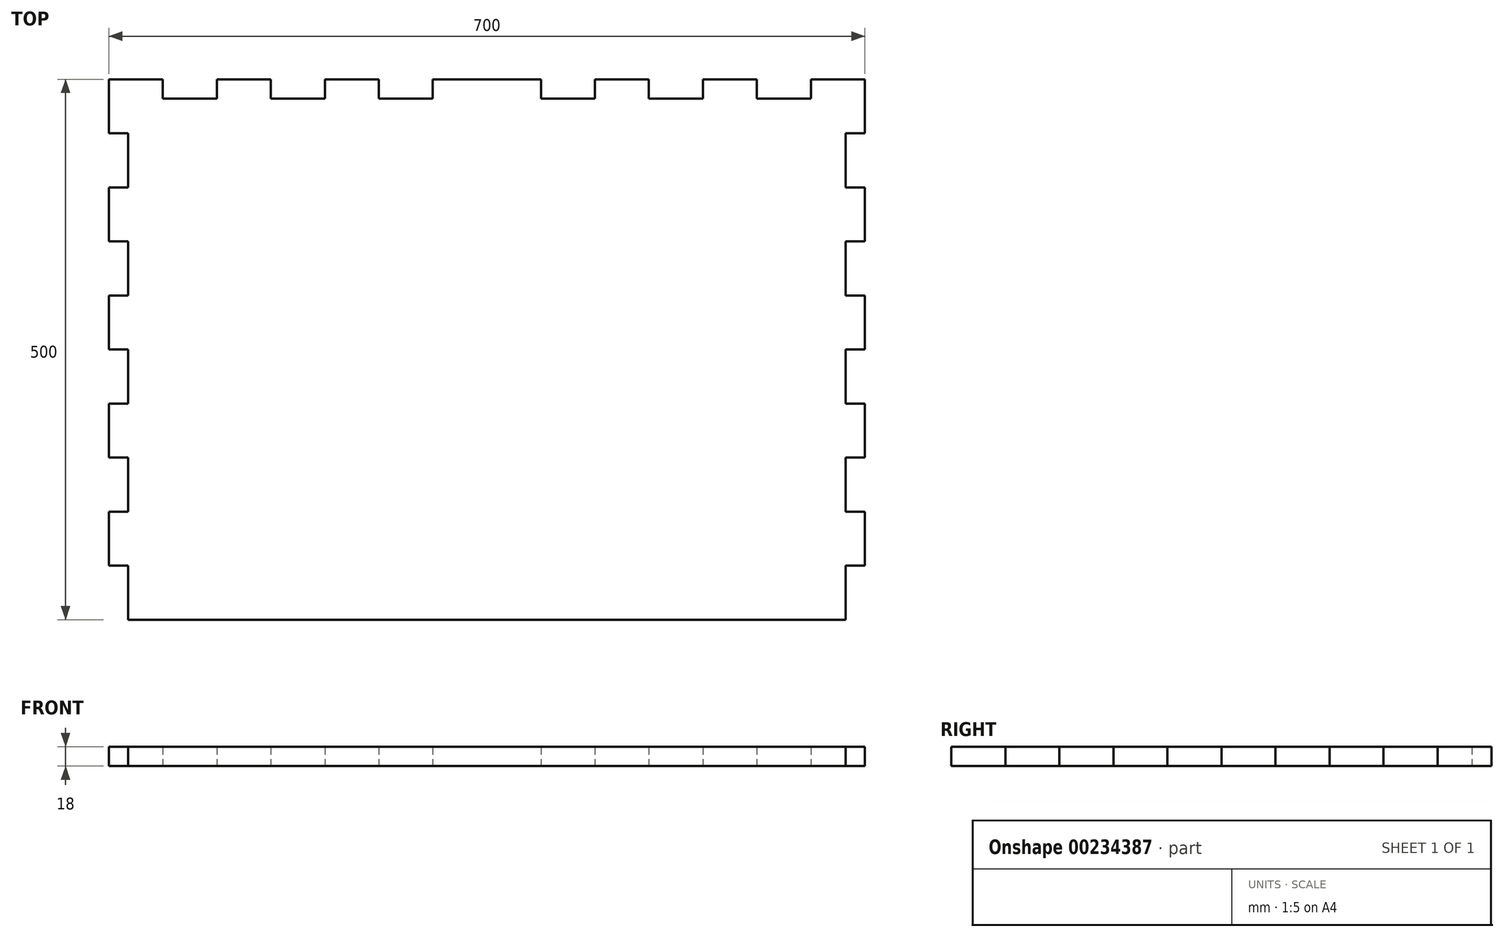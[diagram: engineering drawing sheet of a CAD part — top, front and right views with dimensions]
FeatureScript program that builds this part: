
annotation { "Feature Type Name" : "Feature", "Feature Type Description" : "" }
export const myFeature = defineFeature(function(context is Context, id is Id, definition is map)
    precondition{}
    {
        {
            var Q0;
            Q0=qCreatedBy(makeId("Top.planeOp"),FACE);
            var sketch = newSketch(context, id + "F0", { "sketchPlane" : qUnion([Q0])});
            skLineSegment(sketch, "E0.left", {"start": v(-350, -175) * mm, "end": v(-350, -125) * mm});
            skPoint(sketch, "E0.middle", {"position": v(0, 0) * mm});
            skLineSegment(sketch, "E1.right", {"start": v(-250, 157) * mm, "end": v(-250, 175) * mm});
            skLineSegment(sketch, "E2.right", {"start": v(-200, 157) * mm, "end": v(-200, 175) * mm});
            skLineSegment(sketch, "E3.right", {"start": v(-150, 157) * mm, "end": v(-150, 175) * mm});
            skLineSegment(sketch, "E4.right", {"start": v(-100, 157) * mm, "end": v(-100, 175) * mm});
            skLineSegment(sketch, "E5.right", {"start": v(-50, 157) * mm, "end": v(-50, 175) * mm});
            skLineSegment(sketch, "E6.top", {"start": v(0, 175) * mm, "end": v(50, 175) * mm});
            skLineSegment(sketch, "E6.right", {"start": v(50, 157) * mm, "end": v(50, 175) * mm});
            skLineSegment(sketch, "E7.bottom", {"start": v(50, 157) * mm, "end": v(100, 157) * mm});
            skLineSegment(sketch, "E7.right", {"start": v(100, 157) * mm, "end": v(100, 175) * mm});
            skLineSegment(sketch, "E8.top", {"start": v(100, 175) * mm, "end": v(150, 175) * mm});
            skLineSegment(sketch, "E8.right", {"start": v(150, 157) * mm, "end": v(150, 175) * mm});
            skLineSegment(sketch, "E9.bottom", {"start": v(150, 157) * mm, "end": v(200, 157) * mm});
            skLineSegment(sketch, "E9.right", {"start": v(200, 157) * mm, "end": v(200, 175) * mm});
            skLineSegment(sketch, "E10.top", {"start": v(200, 175) * mm, "end": v(250, 175) * mm});
            skLineSegment(sketch, "E10.right", {"start": v(250, 157) * mm, "end": v(250, 175) * mm});
            skLineSegment(sketch, "E11.bottom", {"start": v(250, 157) * mm, "end": v(300, 157) * mm});
            skLineSegment(sketch, "E11.right", {"start": v(300, 157) * mm, "end": v(300, 175) * mm});
            skLineSegment(sketch, "E12.top", {"start": v(300, 175) * mm, "end": v(350, 175) * mm});
            skLineSegment(sketch, "E12.right", {"start": v(350, 157) * mm, "end": v(350, 175) * mm});
            skPoint(sketch, "E13.orphan", {"position": v(-350, 175) * mm});
            skLineSegment(sketch, "E14.top", {"start": v(-332, -325) * mm, "end": v(332, -325) * mm});
            skLineSegment(sketch, "E14.right", {"start": v(350, -225) * mm, "end": v(350, -275) * mm});
            skLineSegment(sketch, "E15.top", {"start": v(-332, -275) * mm, "end": v(-350, -275) * mm});
            skLineSegment(sketch, "E15.left", {"start": v(-332, -325) * mm, "end": v(-332, -275) * mm});
            skLineSegment(sketch, "E16.top", {"start": v(-332, -225) * mm, "end": v(-350, -225) * mm});
            skLineSegment(sketch, "E16.right", {"start": v(-350, -275) * mm, "end": v(-350, -225) * mm});
            skLineSegment(sketch, "E17.top", {"start": v(-332, -175) * mm, "end": v(-350, -175) * mm});
            skLineSegment(sketch, "E17.left", {"start": v(-332, -225) * mm, "end": v(-332, -175) * mm});
            skLineSegment(sketch, "E18.top", {"start": v(-332, -125) * mm, "end": v(-350, -125) * mm});
            skLineSegment(sketch, "E19.top", {"start": v(-332, -75) * mm, "end": v(-350, -75) * mm});
            skLineSegment(sketch, "E19.left", {"start": v(-332, -125) * mm, "end": v(-332, -75) * mm});
            skLineSegment(sketch, "E20.top", {"start": v(-332, -25) * mm, "end": v(-350, -25) * mm});
            skLineSegment(sketch, "E20.right", {"start": v(-350, -75) * mm, "end": v(-350, -25) * mm});
            skLineSegment(sketch, "E21.top", {"start": v(-332, 25) * mm, "end": v(-350, 25) * mm});
            skLineSegment(sketch, "E21.left", {"start": v(-332, -25) * mm, "end": v(-332, 25) * mm});
            skLineSegment(sketch, "E22.top", {"start": v(-332, 75) * mm, "end": v(-350, 75) * mm});
            skLineSegment(sketch, "E22.right", {"start": v(-350, 25) * mm, "end": v(-350, 75) * mm});
            skLineSegment(sketch, "E23.top", {"start": v(-332, 125) * mm, "end": v(-350, 125) * mm});
            skLineSegment(sketch, "E23.left", {"start": v(-332, 75) * mm, "end": v(-332, 125) * mm});
            skLineSegment(sketch, "E24.trimOffspring", {"start": v(-350, 125) * mm, "end": v(-350, 157) * mm});
            skLineSegment(sketch, "E25.top", {"start": v(332, -275) * mm, "end": v(350, -275) * mm});
            skLineSegment(sketch, "E25.left", {"start": v(332, -325) * mm, "end": v(332, -275) * mm});
            skLineSegment(sketch, "E26.top", {"start": v(332, -225) * mm, "end": v(350, -225) * mm});
            skLineSegment(sketch, "E26.right", {"start": v(350, -275) * mm, "end": v(350, -225) * mm});
            skLineSegment(sketch, "E27.top", {"start": v(332, -175) * mm, "end": v(350, -175) * mm});
            skLineSegment(sketch, "E27.left", {"start": v(332, -225) * mm, "end": v(332, -175) * mm});
            skLineSegment(sketch, "E28.top", {"start": v(332, -125) * mm, "end": v(350, -125) * mm});
            skLineSegment(sketch, "E28.right", {"start": v(350, -175) * mm, "end": v(350, -125) * mm});
            skLineSegment(sketch, "E29.top", {"start": v(332, -75) * mm, "end": v(350, -75) * mm});
            skLineSegment(sketch, "E29.left", {"start": v(332, -125) * mm, "end": v(332, -75) * mm});
            skLineSegment(sketch, "E30.top", {"start": v(332, -25) * mm, "end": v(350, -25) * mm});
            skLineSegment(sketch, "E30.right", {"start": v(350, -75) * mm, "end": v(350, -25) * mm});
            skLineSegment(sketch, "E31.top", {"start": v(332, 25) * mm, "end": v(350, 25) * mm});
            skLineSegment(sketch, "E31.left", {"start": v(332, -25) * mm, "end": v(332, 25) * mm});
            skLineSegment(sketch, "E32.top", {"start": v(332, 75) * mm, "end": v(350, 75) * mm});
            skLineSegment(sketch, "E32.right", {"start": v(350, 25) * mm, "end": v(350, 75) * mm});
            skLineSegment(sketch, "E33.top", {"start": v(332, 125) * mm, "end": v(350, 125) * mm});
            skLineSegment(sketch, "E33.left", {"start": v(332, 75) * mm, "end": v(332, 125) * mm});
            skLineSegment(sketch, "E34.trimOffspring", {"start": v(350, 125) * mm, "end": v(350, 175) * mm});
            skPoint(sketch, "E0.right.start.orphan", {"position": v(350, -175) * mm});
            skPoint(sketch, "E35.orphan", {"position": v(350, -325) * mm});
            skLineSegment(sketch, "E36", {"start": v(-350, 157) * mm, "end": v(-350, 175) * mm});
            skLineSegment(sketch, "E37", {"start": v(-300, 175) * mm, "end": v(-350, 175) * mm});
            skLineSegment(sketch, "E38", {"start": v(-300, 175) * mm, "end": v(-300, 157) * mm});
            skLineSegment(sketch, "E39", {"start": v(-300, 157) * mm, "end": v(-250, 157) * mm});
            skLineSegment(sketch, "E40", {"start": v(-200, 157) * mm, "end": v(-150, 157) * mm});
            skLineSegment(sketch, "E41", {"start": v(-250, 175) * mm, "end": v(-200, 175) * mm});
            skLineSegment(sketch, "E42", {"start": v(-150, 175) * mm, "end": v(-100, 175) * mm});
            skLineSegment(sketch, "E43", {"start": v(-100, 157) * mm, "end": v(-50, 157) * mm});
            skLineSegment(sketch, "E44", {"start": v(-50, 175) * mm, "end": v(0, 175) * mm});
            skSolve(sketch);
        }
        {
            var Q0;
            Q0 = qSketchRegion(id + "F0", true);
            extrude(context, id + "F1", {"entities" : qUnion([Q0]), "depth" : 18 * mm});
        }
    });
